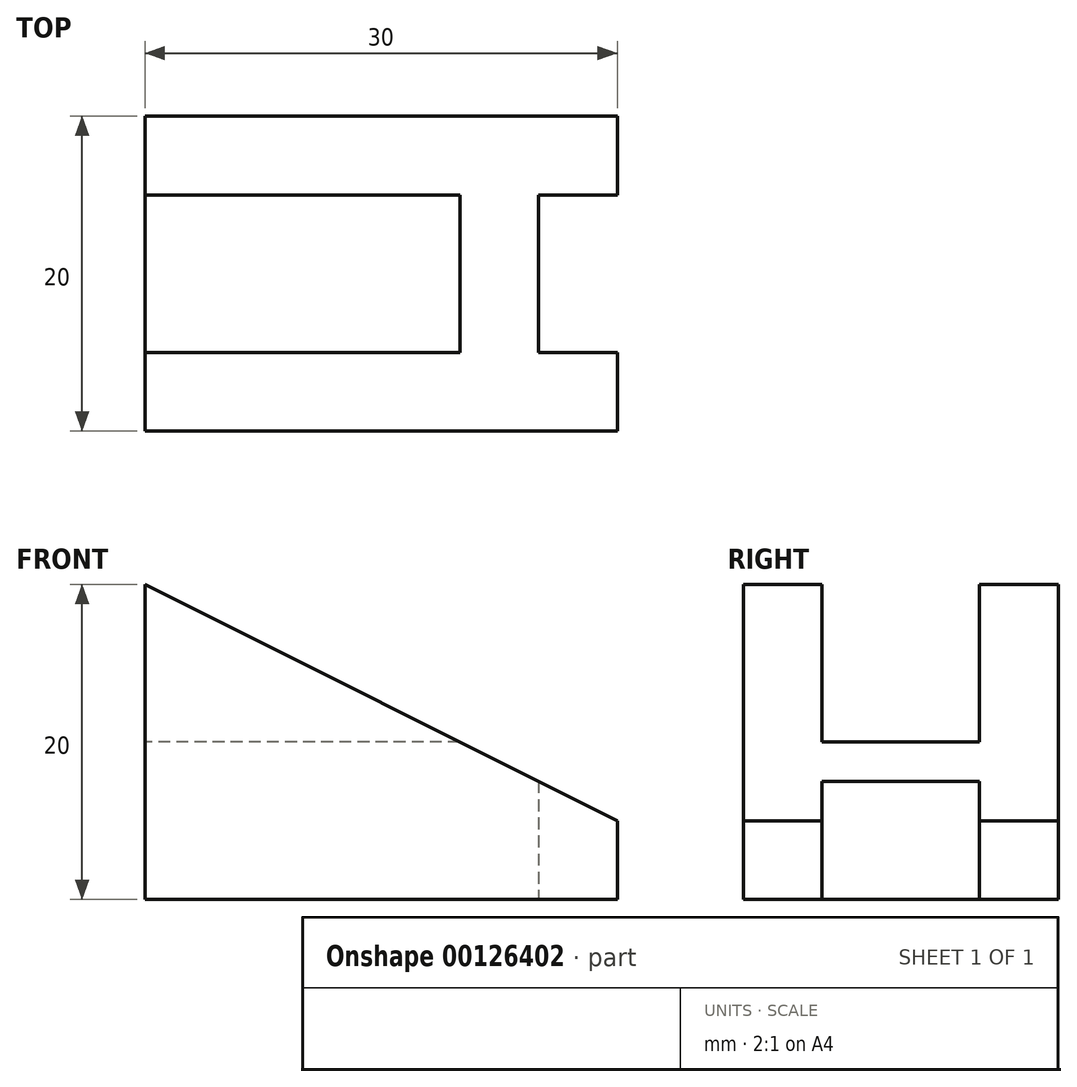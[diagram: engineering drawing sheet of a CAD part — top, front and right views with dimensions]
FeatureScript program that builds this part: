
annotation { "Feature Type Name" : "Feature", "Feature Type Description" : "" }
export const myFeature = defineFeature(function(context is Context, id is Id, definition is map)
    precondition{}
    {
        {
            var Q0;
            Q0=qCreatedBy(makeId("Top.planeOp"),FACE);
            var sketch = newSketch(context, id + "F0", { "sketchPlane" : qUnion([Q0])});
            skLineSegment(sketch, "E0", {"start": v(-15, -10) * mm, "end": v(-15, 0) * mm});
            skLineSegment(sketch, "E1", {"start": v(-15, 0) * mm, "end": v(-15, 10) * mm});
            skLineSegment(sketch, "E2", {"start": v(-15, 10) * mm, "end": v(15, 10) * mm});
            skLineSegment(sketch, "E3", {"start": v(15, -10) * mm, "end": v(-15, -10) * mm});
            skLineSegment(sketch, "E4", {"start": v(15, -10) * mm, "end": v(15, -5) * mm});
            skLineSegment(sketch, "E5", {"start": v(15, -5) * mm, "end": v(10, -5) * mm});
            skLineSegment(sketch, "E6", {"start": v(10, -5) * mm, "end": v(10, 5) * mm});
            skLineSegment(sketch, "E7", {"start": v(10, 5) * mm, "end": v(15, 5) * mm});
            skLineSegment(sketch, "E8", {"start": v(15, 5) * mm, "end": v(15, 10) * mm});
            skSolve(sketch);
        }
        {
            var Q0;
            Q0 = qSketchRegion(id + "F0", true);
            extrude(context, id + "F1", {"entities" : qUnion([Q0]), "depth" : 20 * mm});
        }
        {
            var Q0;
            Q0=makeQuery(id+"F1.opExtrude","SWEPT_FACE",FACE,{"disambiguationData":[OSD([sQuery(id+"F0.wireOp",EDGE,"E3")])]});
            var sketch = newSketch(context, id + "F2", { "sketchPlane" : qUnion([Q0])});
            skLineSegment(sketch, "E9", {"start": v(15, 5) * mm, "end": v(-15, 20) * mm});
            skLineSegment(sketch, "E10", {"start": v(15, 5) * mm, "end": v(15, 20) * mm});
            skLineSegment(sketch, "E11", {"start": v(15, 20) * mm, "end": v(-15, 20) * mm});
            skSolve(sketch);
        }
        {
            var Q0;
            Q0 = qSketchRegion(id + "F2", true);
            extrude(context, id + "F3", {"entities" : qUnion([Q0]), "operationType" : NewBodyOperationType.REMOVE, "endBound" : BoundingType.THROUGH_ALL, "oppositeDirection" : true, "depth" : 25 * mm});
        }
        {
            var Q0;
            Q0=makeQuery(id+"F1.opExtrude","SWEPT_FACE",FACE,{"disambiguationData":[OSD([sQuery(id+"F0.wireOp",EDGE,"E0"),sQuery(id+"F0.wireOp",EDGE,"E1")])]});
            var sketch = newSketch(context, id + "F4", { "sketchPlane" : qUnion([Q0])});
            skLineSegment(sketch, "E12.bottom", {"start": v(5, 20) * mm, "end": v(-5, 20) * mm});
            skLineSegment(sketch, "E12.top", {"start": v(5, 10) * mm, "end": v(-5, 10) * mm});
            skLineSegment(sketch, "E12.left", {"start": v(5, 20) * mm, "end": v(5, 10) * mm});
            skLineSegment(sketch, "E12.right", {"start": v(-5, 20) * mm, "end": v(-5, 10) * mm});
            skPoint(sketch, "E12.middle", {"position": v(0, 15) * mm});
            skSolve(sketch);
        }
        {
            var Q0;
            Q0 = qSketchRegion(id + "F4", true);
            extrude(context, id + "F5", {"entities" : qUnion([Q0]), "operationType" : NewBodyOperationType.REMOVE, "endBound" : BoundingType.THROUGH_ALL, "oppositeDirection" : true, "depth" : 25 * mm});
        }
    });
